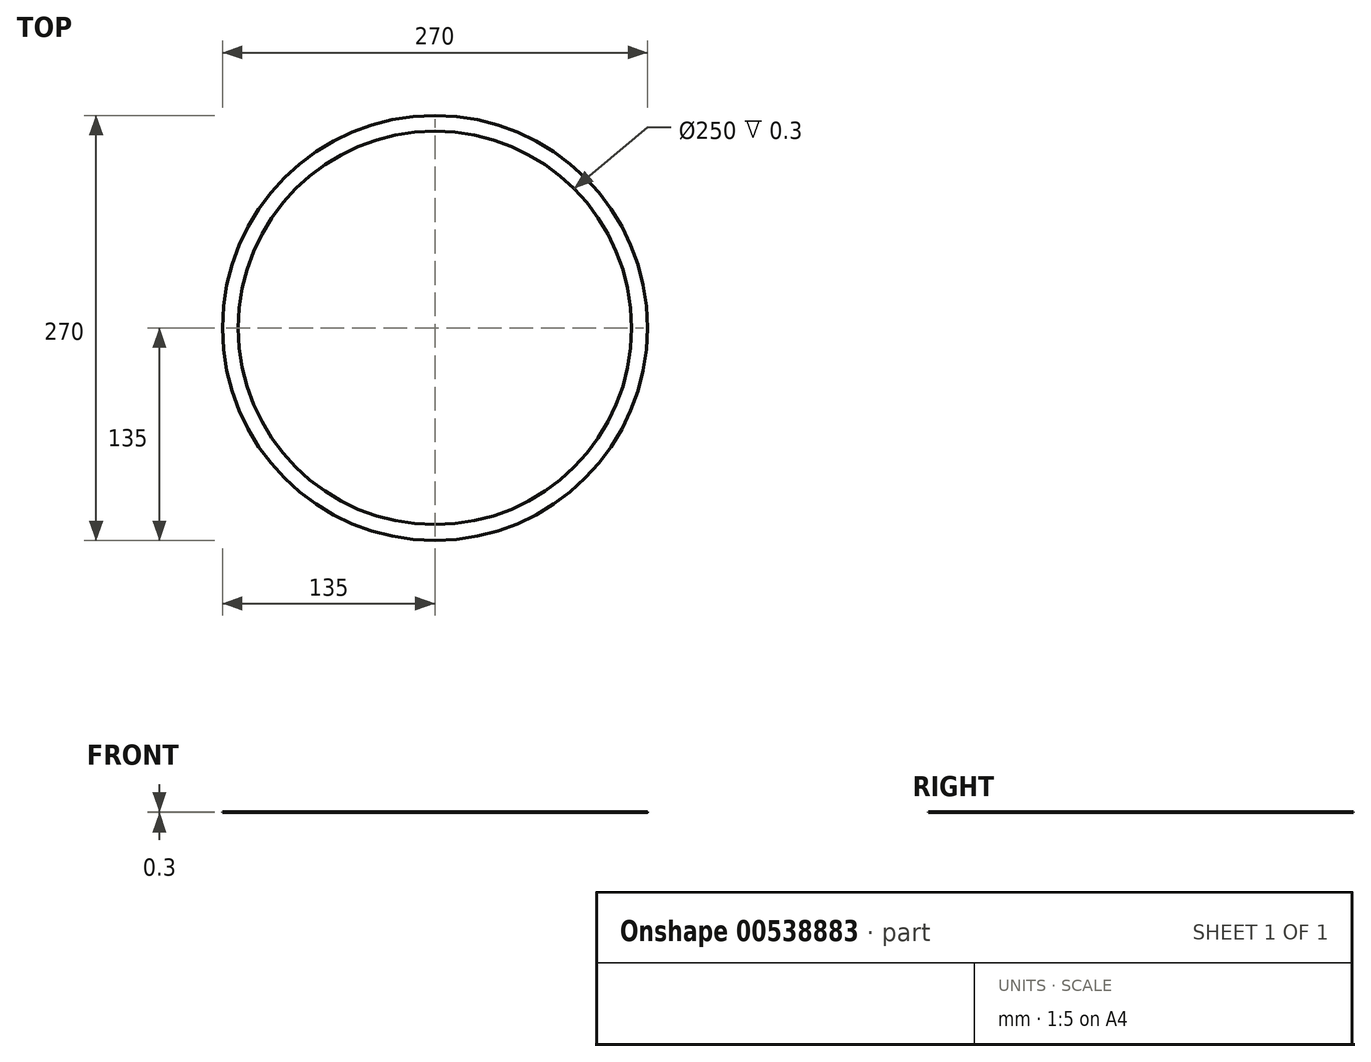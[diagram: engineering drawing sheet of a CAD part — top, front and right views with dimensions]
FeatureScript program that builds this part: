
annotation { "Feature Type Name" : "Feature", "Feature Type Description" : "" }
export const myFeature = defineFeature(function(context is Context, id is Id, definition is map)
    precondition{}
    {
        {
            var Q0;
            Q0=qCreatedBy(makeId("Top.planeOp"),FACE);
            var sketch = newSketch(context, id + "F0", { "sketchPlane" : qUnion([Q0])});
            skCircle(sketch, "E0", {"center": v(0, 0) * mm, "radius": 135 * mm});
            skSolve(sketch);
        }
        {
            var Q0;
            Q0=makeQuery(id+"F0.imprint","IMPRINT",FACE,{"disambiguationData":[TD([[makeQuery(id+"F0.imprint","IMPRINT",EDGE,{"derivedFrom":sQuery(id+"F0.wireOp",EDGE,"E0")}),1.0]])]});
            extrude(context, id + "F1", {"entities" : qUnion([Q0]), "depth" : .3 * mm, "offsetDistance" : 25 * mm});
        }
        {
            var Q0;
            Q0=makeQuery(id+"F1.opExtrude","CAP_FACE",FACE,{"disambiguationData":[OSD([sQuery(id+"F0.wireOp",EDGE,"E0")])],"isStart":false});
            var sketch = newSketch(context, id + "F2", { "sketchPlane" : qUnion([Q0])});
            skCircle(sketch, "E1", {"center": v(0, 0) * mm, "radius": 125 * mm});
            skSolve(sketch);
        }
        {
            var Q0;
            Q0 = qSketchRegion(id + "F2", true);
            extrude(context, id + "F3", {"entities" : qUnion([Q0]), "operationType" : NewBodyOperationType.REMOVE, "oppositeDirection" : true, "depth" : 25 * mm, "offsetDistance" : 25 * mm});
        }
    });
